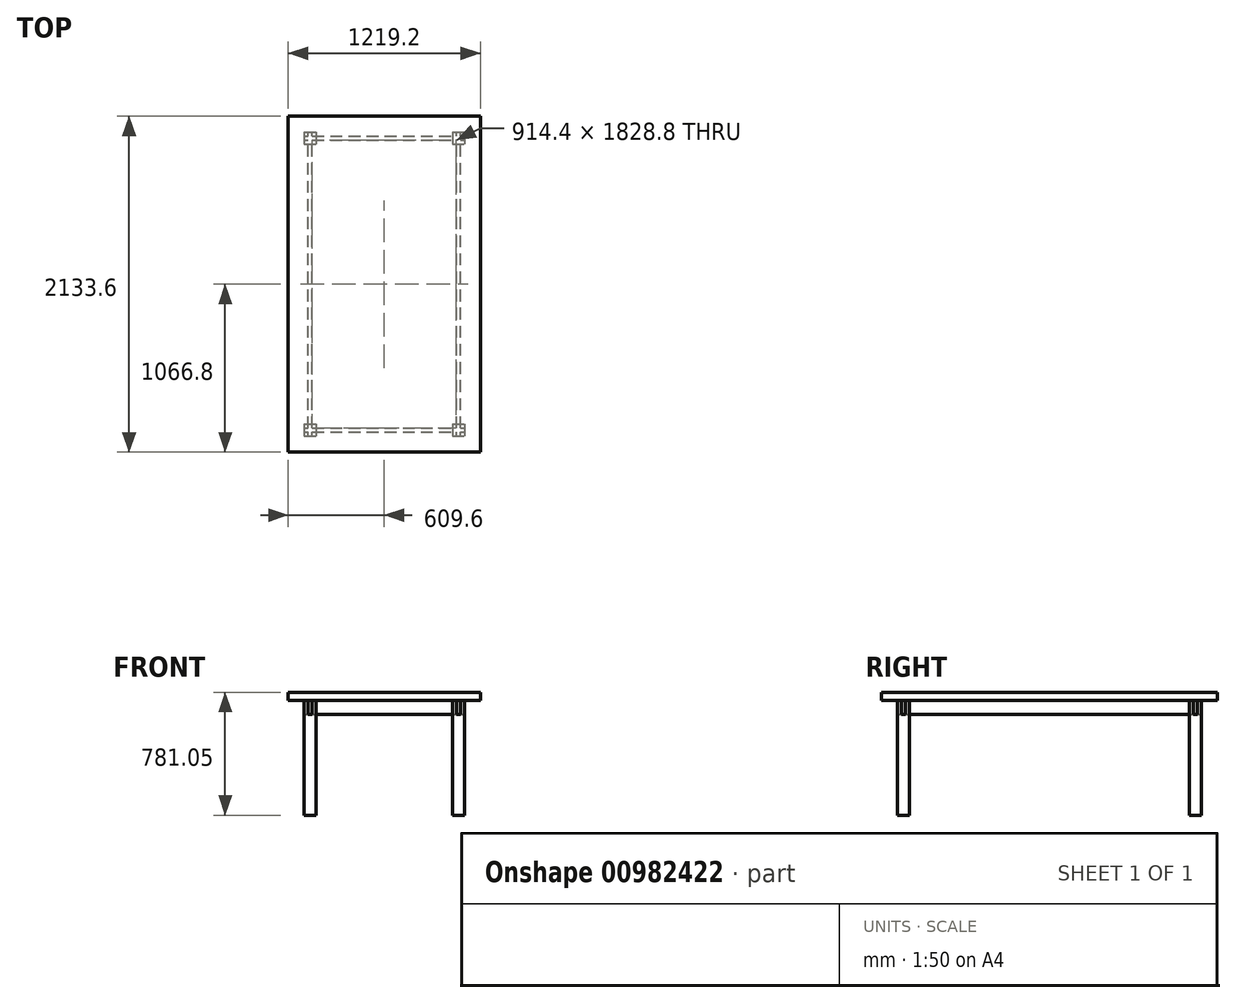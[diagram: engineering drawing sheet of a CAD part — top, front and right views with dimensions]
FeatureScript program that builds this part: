
annotation { "Feature Type Name" : "Feature", "Feature Type Description" : "" }
export const myFeature = defineFeature(function(context is Context, id is Id, definition is map)
    precondition{}
    {
        {
            var Q0;
            Q0=qCreatedBy(makeId("Top.planeOp"),FACE);
            var sketch = newSketch(context, id + "F0", { "sketchPlane" : qUnion([Q0])});
            skLineSegment(sketch, "E0.bottom", {"start": v(-609.6, 1066.8) * mm, "end": v(609.6, 1066.8) * mm});
            skLineSegment(sketch, "E0.top", {"start": v(-609.6, -1066.8) * mm, "end": v(609.6, -1066.8) * mm});
            skLineSegment(sketch, "E0.left", {"start": v(-609.6, 1066.8) * mm, "end": v(-609.6, -1066.8) * mm});
            skLineSegment(sketch, "E0.right", {"start": v(609.6, 1066.8) * mm, "end": v(609.6, -1066.8) * mm});
            skLineSegment(sketch, "E1", {"start": v(-609.6, 1066.8) * mm, "end": v(609.6, -1066.8) * mm, "construction": true});
            skSolve(sketch);
        }
        {
            var Q0;
            Q0=qSketchRegion(id+"F0",true);
            extrude(context, id + "F1", {"entities" : qUnion([Q0]), "depth" : 50.8 * mm, "offsetDistance" : 25.4 * mm});
        }
        {
            var Q0;
            Q0=makeQuery(id+"F1.opExtrude","CAP_FACE",FACE,{"disambiguationData":[OSD([sQuery(id+"F0.wireOp",EDGE,"E0.bottom"),sQuery(id+"F0.wireOp",EDGE,"E0.top"),sQuery(id+"F0.wireOp",EDGE,"E0.left"),sQuery(id+"F0.wireOp",EDGE,"E0.right")])],"isStart":true});
            var sketch = newSketch(context, id + "F2", { "sketchPlane" : qUnion([Q0])});
            skLineSegment(sketch, "E2.bottom", {"start": v(-469.9, -927.1) * mm, "end": v(469.9, -927.1) * mm, "construction": true});
            skLineSegment(sketch, "E2.top", {"start": v(-469.9, 927.1) * mm, "end": v(469.9, 927.1) * mm, "construction": true});
            skLineSegment(sketch, "E2.left", {"start": v(-469.9, -927.1) * mm, "end": v(-469.9, 927.1) * mm, "construction": true});
            skLineSegment(sketch, "E2.right", {"start": v(469.9, -927.1) * mm, "end": v(469.9, 927.1) * mm, "construction": true});
            skPoint(sketch, "E2.middle", {"position": v(0, 0) * mm});
            skLineSegment(sketch, "E3.bottom", {"start": v(-508, -965.2) * mm, "end": v(-431.8, -965.2) * mm});
            skLineSegment(sketch, "E3.top", {"start": v(-508, -889) * mm, "end": v(-431.8, -889) * mm});
            skLineSegment(sketch, "E3.left", {"start": v(-508, -965.2) * mm, "end": v(-508, -889) * mm});
            skLineSegment(sketch, "E3.right", {"start": v(-431.8, -965.2) * mm, "end": v(-431.8, -889) * mm});
            skPoint(sketch, "E3.middle", {"position": v(-469.9, -927.1) * mm});
            skLineSegment(sketch, "E4.bottom", {"start": v(431.8, -965.2) * mm, "end": v(508, -965.2) * mm});
            skLineSegment(sketch, "E4.top", {"start": v(431.8, -889) * mm, "end": v(508, -889) * mm});
            skLineSegment(sketch, "E4.left", {"start": v(431.8, -965.2) * mm, "end": v(431.8, -889) * mm});
            skLineSegment(sketch, "E4.right", {"start": v(508, -965.2) * mm, "end": v(508, -889) * mm});
            skPoint(sketch, "E4.middle", {"position": v(469.9, -927.1) * mm});
            skLineSegment(sketch, "E5.bottom", {"start": v(-508, 889) * mm, "end": v(-431.8, 889) * mm});
            skLineSegment(sketch, "E5.top", {"start": v(-508, 965.2) * mm, "end": v(-431.8, 965.2) * mm});
            skLineSegment(sketch, "E5.left", {"start": v(-508, 889) * mm, "end": v(-508, 965.2) * mm});
            skLineSegment(sketch, "E5.right", {"start": v(-431.8, 889) * mm, "end": v(-431.8, 965.2) * mm});
            skPoint(sketch, "E5.middle", {"position": v(-469.9, 927.1) * mm});
            skLineSegment(sketch, "E6.bottom", {"start": v(431.8, 889) * mm, "end": v(508, 889) * mm});
            skLineSegment(sketch, "E6.top", {"start": v(431.8, 965.2) * mm, "end": v(508, 965.2) * mm});
            skLineSegment(sketch, "E6.left", {"start": v(431.8, 889) * mm, "end": v(431.8, 965.2) * mm});
            skLineSegment(sketch, "E6.right", {"start": v(508, 889) * mm, "end": v(508, 965.2) * mm});
            skPoint(sketch, "E6.middle", {"position": v(469.9, 927.1) * mm});
            skSolve(sketch);
        }
        {
            var Q0;
            Q0=qSketchRegion(id+"F2",true);
            extrude(context, id + "F3", {"entities" : qUnion([Q0]), "depth" : 730.25 * mm, "offsetDistance" : 25.4 * mm});
        }
        {
            var Q0;
            Q0=makeQuery(id+"F2.imprint","IMPRINT",FACE,{"disambiguationData":[TD([[makeQuery(id+"F2.imprint","IMPRINT",EDGE,{"derivedFrom":sQuery(id+"F2.wireOp",EDGE,"E3.bottom")}),-1.0]])]});
            var sketch = newSketch(context, id + "F4", { "sketchPlane" : qUnion([Q0])});
            skLineSegment(sketch, "E7.bottom", {"start": v(-508, -914.4) * mm, "end": v(508, -914.4) * mm});
            skLineSegment(sketch, "E7.top", {"start": v(-508, -939.8) * mm, "end": v(508, -939.8) * mm});
            skLineSegment(sketch, "E7.left", {"start": v(-508, -914.4) * mm, "end": v(-508, -939.8) * mm});
            skLineSegment(sketch, "E7.right", {"start": v(508, -914.4) * mm, "end": v(508, -939.8) * mm});
            skPoint(sketch, "E7.middle", {"position": v(0, -927.1) * mm});
            skLineSegment(sketch, "E8.bottom", {"start": v(-457.2, 965.2) * mm, "end": v(-482.6, 965.2) * mm});
            skLineSegment(sketch, "E8.top", {"start": v(-457.2, -965.2) * mm, "end": v(-482.6, -965.2) * mm});
            skLineSegment(sketch, "E8.left", {"start": v(-457.2, 965.2) * mm, "end": v(-457.2, -965.2) * mm});
            skLineSegment(sketch, "E8.right", {"start": v(-482.6, 965.2) * mm, "end": v(-482.6, -965.2) * mm});
            skPoint(sketch, "E8.middle", {"position": v(-469.9, 0) * mm});
            skLineSegment(sketch, "E9.bottom", {"start": v(-508, 939.8) * mm, "end": v(508, 939.8) * mm});
            skLineSegment(sketch, "E9.top", {"start": v(-508, 914.4) * mm, "end": v(508, 914.4) * mm});
            skLineSegment(sketch, "E9.left", {"start": v(-508, 939.8) * mm, "end": v(-508, 914.4) * mm});
            skLineSegment(sketch, "E9.right", {"start": v(508, 939.8) * mm, "end": v(508, 914.4) * mm});
            skPoint(sketch, "E9.middle", {"position": v(0, 927.1) * mm});
            skLineSegment(sketch, "E10.bottom", {"start": v(482.6, 965.2) * mm, "end": v(457.2, 965.2) * mm});
            skLineSegment(sketch, "E10.top", {"start": v(482.6, -965.2) * mm, "end": v(457.2, -965.2) * mm});
            skLineSegment(sketch, "E10.left", {"start": v(482.6, 965.2) * mm, "end": v(482.6, -965.2) * mm});
            skLineSegment(sketch, "E10.right", {"start": v(457.2, 965.2) * mm, "end": v(457.2, -965.2) * mm});
            skPoint(sketch, "E10.middle", {"position": v(469.9, 0) * mm});
            skSolve(sketch);
        }
        {
            var Q0;
            Q0=qSketchRegion(id+"F4",true);
            extrude(context, id + "F5", {"entities" : qUnion([Q0]), "depth" : 88.9 * mm, "offsetDistance" : 25.4 * mm});
        }
    });
